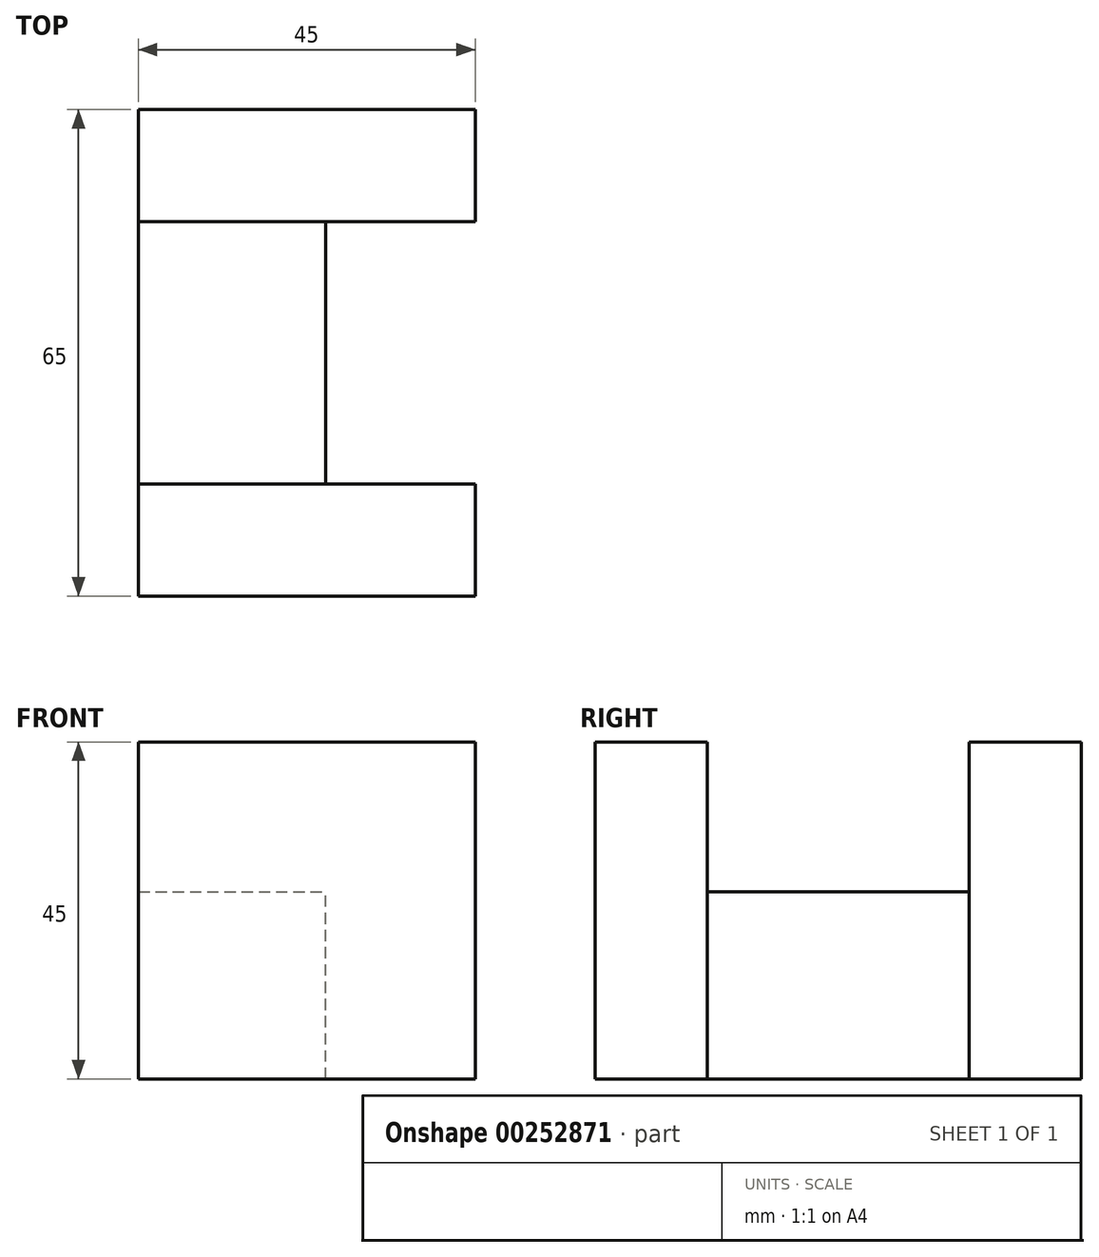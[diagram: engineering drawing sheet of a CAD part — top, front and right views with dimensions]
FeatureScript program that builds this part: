
annotation { "Feature Type Name" : "Feature", "Feature Type Description" : "" }
export const myFeature = defineFeature(function(context is Context, id is Id, definition is map)
    precondition{}
    {
        {
            var Q0;
            Q0=qCreatedBy(makeId("Front.planeOp"),FACE);
            var sketch = newSketch(context, id + "F0", { "sketchPlane" : qUnion([Q0])});
            skLineSegment(sketch, "E0.bottom", {"start": v(0, 0) * mm, "end": v(25, 0) * mm});
            skLineSegment(sketch, "E0.top", {"start": v(0, 25) * mm, "end": v(25, 25) * mm});
            skLineSegment(sketch, "E0.left", {"start": v(0, 0) * mm, "end": v(0, 25) * mm});
            skLineSegment(sketch, "E0.right", {"start": v(25, 0) * mm, "end": v(25, 25) * mm});
            skSolve(sketch);
        }
        {
            var Q0;
            Q0=makeQuery(id+"F0.imprint","IMPRINT",FACE,{"disambiguationData":[TD([[makeQuery(id+"F0.imprint","IMPRINT",EDGE,{"derivedFrom":sQuery(id+"F0.wireOp",EDGE,"E0.bottom")}),1.0]])]});
            extrude(context, id + "F1", {"entities" : qUnion([Q0]), "depth" : 17.5 * mm});
        }
        {
            var Q0;
            Q0=makeQuery(id+"F1.opExtrude","CAP_FACE",FACE,{"disambiguationData":[OSD([sQuery(id+"F0.wireOp",EDGE,"E0.bottom"),sQuery(id+"F0.wireOp",EDGE,"E0.top"),sQuery(id+"F0.wireOp",EDGE,"E0.left"),sQuery(id+"F0.wireOp",EDGE,"E0.right")])],"isStart":false});
            var sketch = newSketch(context, id + "F2", { "sketchPlane" : qUnion([Q0])});
            skLineSegment(sketch, "E1.bottom", {"start": v(0, 0) * mm, "end": v(45, 0) * mm});
            skLineSegment(sketch, "E1.top", {"start": v(0, 45) * mm, "end": v(45, 45) * mm});
            skLineSegment(sketch, "E1.left", {"start": v(0, 0) * mm, "end": v(0, 45) * mm});
            skLineSegment(sketch, "E1.right", {"start": v(45, 0) * mm, "end": v(45, 45) * mm});
            skSolve(sketch);
        }
        {
            var Q0;
            {var subQ3=sQuery(id+"F2.wireOp",EDGE,"E1.top");Q0=makeQuery(id+"F2.imprint","IMPRINT",FACE,{"disambiguationData":[TD([[makeQuery(id+"F2.imprint","IMPRINT",EDGE,{"derivedFrom":subQ3}),-1.0]])]});}
            var Q1;
            {var subQ4=makeQuery(id+"F1.opExtrude","CAP_EDGE",EDGE,{"disambiguationData":[OSD([sQuery(id+"F0.wireOp",EDGE,"E0.top")])],"isStart":false});Q1=makeQuery(id+"F2.imprint","IMPRINT",FACE,{"disambiguationData":[TD([[makeQuery(id+"F2.imprint","IMPRINT",EDGE,{"derivedFrom":subQ4}),-1.0]])]});}
            extrude(context, id + "F3", {"entities" : qUnion([Q0, Q1]), "operationType" : NewBodyOperationType.ADD, "depth" : 15 * mm, "offsetDistance" : 25 * mm});
        }
        {
            var Q0;
            Q0=makeQuery(id+"F1.opExtrude","SWEPT_BODY",BODY,{"disambiguationData":[OSD([sQuery(id+"F0.wireOp",EDGE,"E0.bottom"),sQuery(id+"F0.wireOp",EDGE,"E0.top"),sQuery(id+"F0.wireOp",EDGE,"E0.left"),sQuery(id+"F0.wireOp",EDGE,"E0.right")])]});
            var Q1;
            Q1=makeQuery(id+"F1.opExtrude","CAP_FACE",FACE,{"disambiguationData":[OSD([sQuery(id+"F0.wireOp",EDGE,"E0.bottom"),sQuery(id+"F0.wireOp",EDGE,"E0.top"),sQuery(id+"F0.wireOp",EDGE,"E0.left"),sQuery(id+"F0.wireOp",EDGE,"E0.right")])],"isStart":true});
            mirror(context, id + "F4", {"operationType" : NewBodyOperationType.ADD, "entities" : qUnion([Q0]), "mirrorPlane" : qUnion([Q1])});
        }
    });
